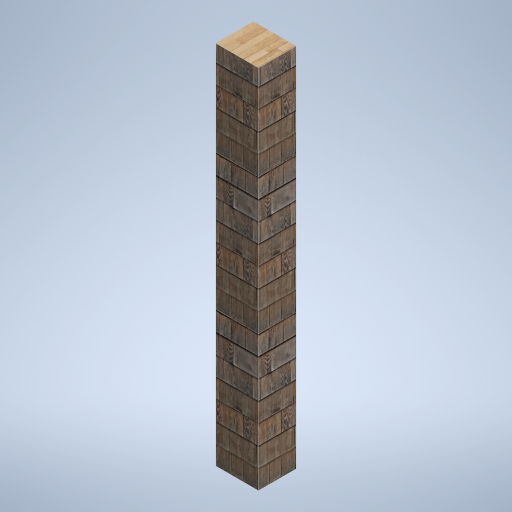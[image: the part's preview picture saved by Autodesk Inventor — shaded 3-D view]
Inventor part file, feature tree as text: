
AUTODESK INVENTOR PART (.ipt)
format: ipt  version: 2024.2 (Build 282272000, 272)  size: 343,552 bytes
history: native  units: in
note: dims shown in document units (in); Inventor stores cm internally (conversion verified against a paired STEP export)
features: other x3, sketch x1
ambient origin geometry x8: Origin, YZ Plane, XZ Plane, XY Plane, X Axis, Y Axis, Z Axis, Center Point
bodies: Solid1 (feature_tree)
feature tree (4):
  other  "support_column_01.ipt"
  other  "Solid1::support_column_01.ipt"
  other  "TaggingFeature1"
  sketch  "Sketch1"  dims[d0=0.3937in]
